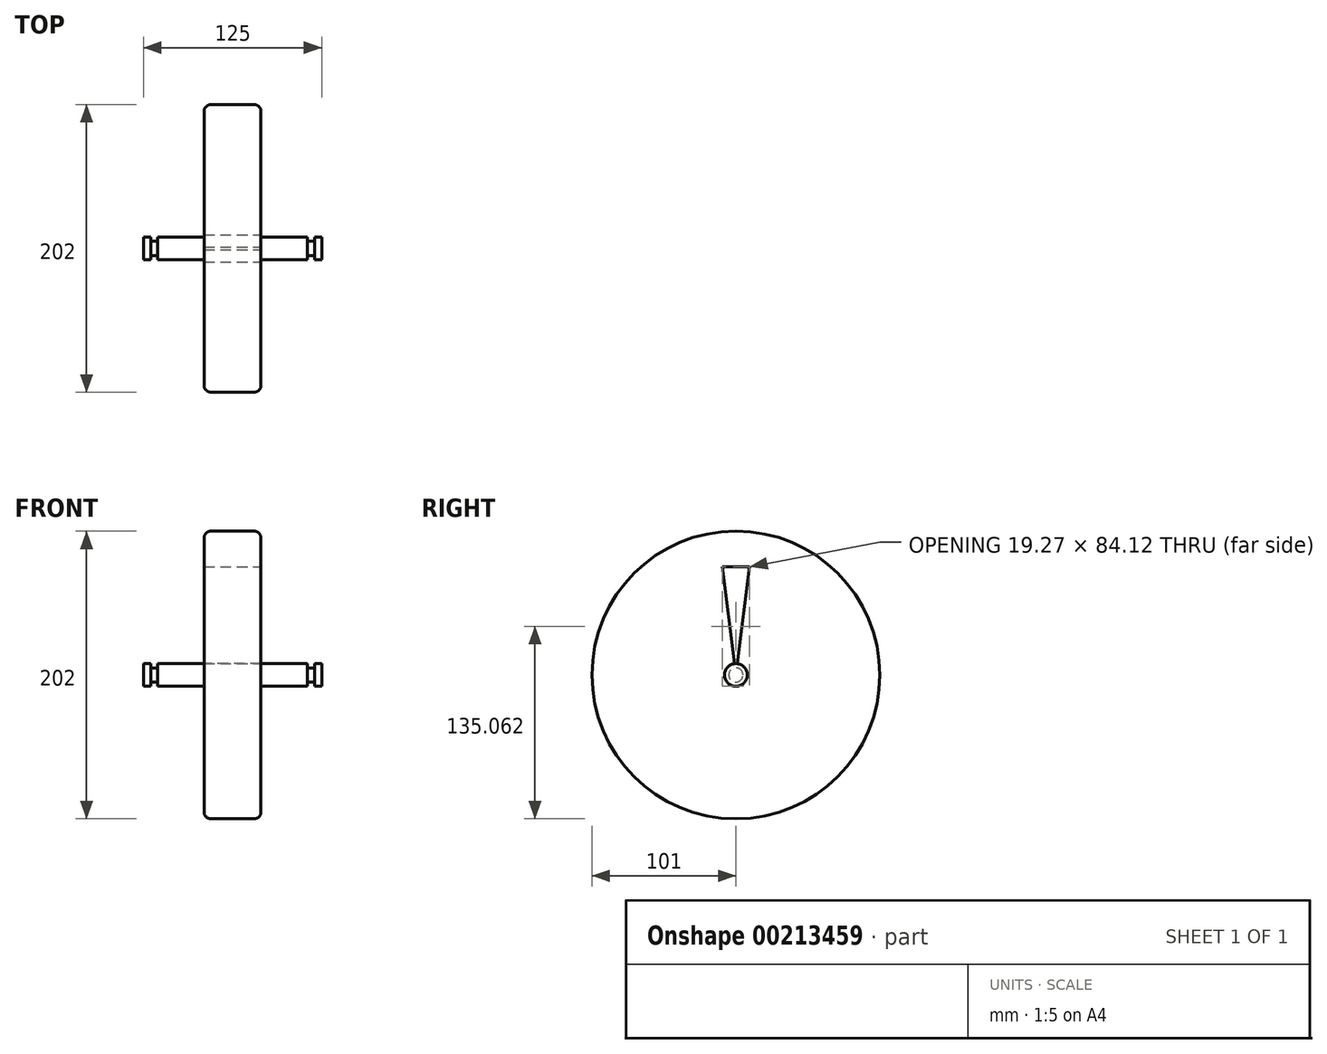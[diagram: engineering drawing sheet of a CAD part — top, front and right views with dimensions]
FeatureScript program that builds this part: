
annotation { "Feature Type Name" : "Feature", "Feature Type Description" : "" }
export const myFeature = defineFeature(function(context is Context, id is Id, definition is map)
    precondition{}
    {
        {
            var Q0;
            Q0=qCreatedBy(makeId("Front.planeOp"),FACE);
            var sketch = newSketch(context, id + "F0", { "sketchPlane" : qUnion([Q0])});
            skLineSegment(sketch, "E0", {"start": v(-87.22, 0) * mm, "end": v(73.7, 0) * mm, "construction": true});
            skLineSegment(sketch, "E1.bottom", {"start": v(-62.5, 8) * mm, "end": v(-57.5, 8) * mm});
            skLineSegment(sketch, "E1.top", {"start": v(-62.5, 0) * mm, "end": v(62.5, 0) * mm});
            skLineSegment(sketch, "E1.left", {"start": v(-62.5, 8) * mm, "end": v(-62.5, 0) * mm});
            skLineSegment(sketch, "E1.right", {"start": v(62.5, 8) * mm, "end": v(62.5, 0) * mm});
            skLineSegment(sketch, "E2.bottom", {"start": v(-15.1, 101) * mm, "end": v(14.9, 101) * mm});
            skLineSegment(sketch, "E2.top", {"start": v(-20.1, 0) * mm, "end": v(19.9, 0) * mm});
            skLineSegment(sketch, "E2.left", {"start": v(-20.1, 96) * mm, "end": v(-20.1, 8) * mm});
            skLineSegment(sketch, "E2.right", {"start": v(19.9, 96) * mm, "end": v(19.9, 8) * mm});
            skLineSegment(sketch, "E3", {"start": v(0, 0) * mm, "end": v(-0.1, 115.13) * mm, "construction": true});
            skPoint(sketch, "E3.endSnap0", {"position": v(-0.1, 101) * mm});
            skPoint(sketch, "E4.visualSharp", {"position": v(-20.1, 101) * mm});
            skArc(sketch, "E4.filletArc", {"start": v(-15.1, 101) * mm, "mid": v(-18.64, 99.54) * mm, "end": v(-20.1, 96) * mm});
            skPoint(sketch, "E5.visualSharp", {"position": v(19.9, 101) * mm});
            skArc(sketch, "E5.filletArc", {"start": v(19.9, 96) * mm, "mid": v(18.43, 99.54) * mm, "end": v(14.9, 101) * mm});
            skLineSegment(sketch, "E6.0", {"start": v(-52.5, 8) * mm, "end": v(-52.5, 5) * mm});
            skLineSegment(sketch, "E7.0", {"start": v(52.5, 8) * mm, "end": v(52.5, 5) * mm});
            skLineSegment(sketch, "E8.0", {"start": v(-57.5, 8) * mm, "end": v(-57.5, 5) * mm});
            skLineSegment(sketch, "E9.0", {"start": v(57.5, 8) * mm, "end": v(57.5, 5) * mm});
            skLineSegment(sketch, "E10.0", {"start": v(-57.5, 5) * mm, "end": v(-52.5, 5) * mm});
            skLineSegment(sketch, "E11.trimOffspring", {"start": v(52.5, 5) * mm, "end": v(57.5, 5) * mm});
            skLineSegment(sketch, "E12.trimOffspring", {"start": v(57.5, 8) * mm, "end": v(62.5, 8) * mm});
            skLineSegment(sketch, "E13.trimOffspring", {"start": v(-52.5, 8) * mm, "end": v(-20.1, 8) * mm});
            skLineSegment(sketch, "E14.trimOffspring", {"start": v(19.9, 8) * mm, "end": v(52.5, 8) * mm});
            skSolve(sketch);
        }
        {
            var Q0;
            Q0=makeQuery(id+"F0.imprint","IMPRINT",FACE,{"disambiguationData":[TD([[makeQuery(id+"F0.imprint","IMPRINT",EDGE,{"derivedFrom":sQuery(id+"F0.wireOp",EDGE,"E1.bottom")}),-1.0]])]});
            var Q1;
            Q1=sQuery(id+"F0.wireOp",EDGE,"E0");
            revolve(context, id + "F1", {"entities" : qUnion([Q0]), "axis" : qUnion([Q1]), "revolveType" : RevolveType.FULL});
        }
        {
            var Q0;
            Q0=makeQuery(id+"F1.opRevolve","SWEPT_FACE",FACE,{"disambiguationData":[OSD([sQuery(id+"F0.wireOp",EDGE,"E2.right")])]});
            var sketch = newSketch(context, id + "F2", { "sketchPlane" : qUnion([Q0])});
            skLineSegment(sketch, "E15", {"start": v(0, 0) * mm, "end": v(-9.64, 76.12) * mm});
            skLineSegment(sketch, "E16", {"start": v(-9.64, 76.12) * mm, "end": v(0, 76.12) * mm});
            skLineSegment(sketch, "E17", {"start": v(0, 0) * mm, "end": v(0, 38.74) * mm, "construction": true});
            skLineSegment(sketch, "E18.MirrorCS", {"start": v(0, 0) * mm, "end": v(9.64, 76.12) * mm});
            skLineSegment(sketch, "E19.MirrorCS", {"start": v(9.64, 76.12) * mm, "end": v(0, 76.12) * mm});
            skSolve(sketch);
        }
        {
            var Q0;
            {var subQ4=sQuery(id+"F2.wireOp",EDGE,"E16");Q0=makeQuery(id+"F2.imprint","IMPRINT",FACE,{"disambiguationData":[TD([[makeQuery(id+"F2.imprint","IMPRINT",EDGE,{"derivedFrom":subQ4}),-1.0]])]});}
            extrude(context, id + "F3", {"entities" : qUnion([Q0]), "operationType" : NewBodyOperationType.REMOVE, "endBound" : BoundingType.THROUGH_ALL, "oppositeDirection" : true, "depth" : 5 * mm});
        }
    });
